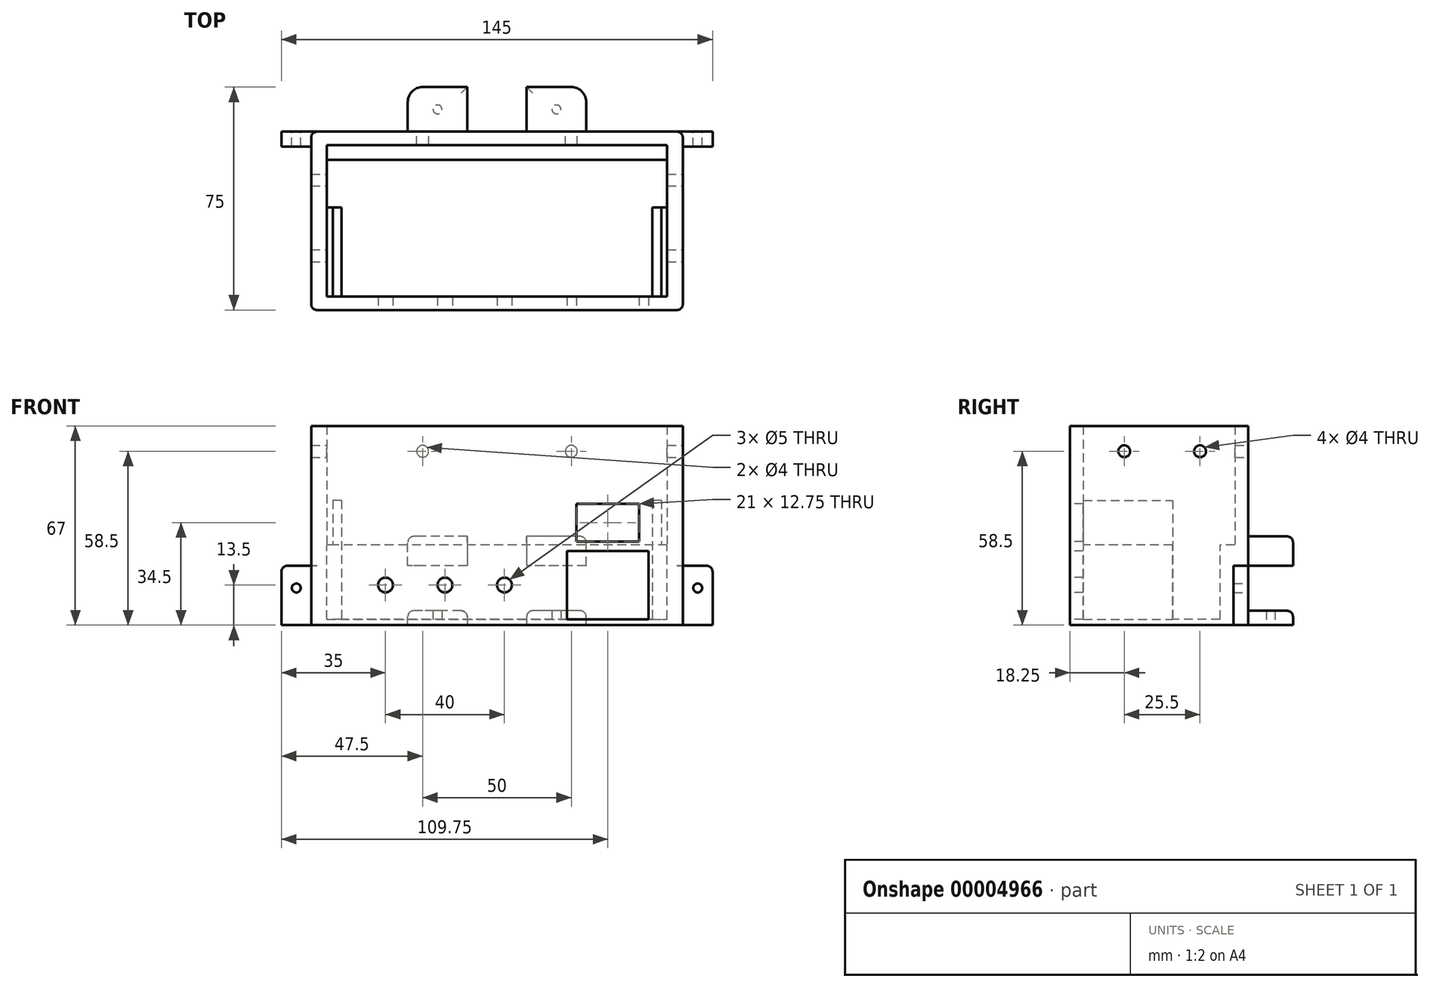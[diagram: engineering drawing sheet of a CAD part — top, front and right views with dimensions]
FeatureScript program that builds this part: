
annotation { "Feature Type Name" : "Feature", "Feature Type Description" : "" }
export const myFeature = defineFeature(function(context is Context, id is Id, definition is map)
    precondition{}
    {
        {
            var Q0;
            Q0=qCreatedBy(makeId("Top.planeOp"),FACE);
            var sketch = newSketch(context, id + "F0", { "sketchPlane" : qUnion([Q0])});
            skLineSegment(sketch, "E0.rect.bottom", {"start": v(57.25, 25.5) * mm, "end": v(-57.25, 25.5) * mm});
            skLineSegment(sketch, "E0.rect.top", {"start": v(57.25, -25.5) * mm, "end": v(-57.25, -25.5) * mm});
            skLineSegment(sketch, "E0.rect.left", {"start": v(57.25, 25.5) * mm, "end": v(57.25, -25.5) * mm});
            skLineSegment(sketch, "E0.rect.right", {"start": v(-57.25, 25.5) * mm, "end": v(-57.25, -25.5) * mm});
            skPoint(sketch, "E0.rect.middle", {"position": v(0, 0) * mm});
            skLineSegment(sketch, "E1.rect.bottom", {"start": v(62.5, 30) * mm, "end": v(-62.5, 30) * mm});
            skLineSegment(sketch, "E1.rect.top", {"start": v(62.5, -30) * mm, "end": v(-62.5, -30) * mm});
            skLineSegment(sketch, "E1.rect.left", {"start": v(62.5, 30) * mm, "end": v(62.5, -30) * mm});
            skLineSegment(sketch, "E1.rect.right", {"start": v(-62.5, 30) * mm, "end": v(-62.5, -30) * mm});
            skSolve(sketch);
        }
        {
            var Q0;
            Q0 = qSketchRegion(id + "F0", true);
            extrude(context, id + "F1", {"entities" : qUnion([Q0]), "depth" : 40 * mm});
        }
        {
            var Q0;
            Q0=makeQuery(id+"F1.opExtrude","CAP_FACE",FACE,{"disambiguationData":[OSD([sQuery(id+"F0.wireOp",EDGE,"E0.rect.bottom"),sQuery(id+"F0.wireOp",EDGE,"E0.rect.top"),sQuery(id+"F0.wireOp",EDGE,"E0.rect.left"),sQuery(id+"F0.wireOp",EDGE,"E0.rect.right"),sQuery(id+"F0.wireOp",EDGE,"E1.rect.bottom"),sQuery(id+"F0.wireOp",EDGE,"E1.rect.top"),sQuery(id+"F0.wireOp",EDGE,"E1.rect.left"),sQuery(id+"F0.wireOp",EDGE,"E1.rect.right")])],"isStart":true});
            var sketch = newSketch(context, id + "F2", { "sketchPlane" : qUnion([Q0])});
            skLineSegment(sketch, "E2", {"start": v(0, 0) * mm, "end": v(0, 25.5) * mm, "construction": true});
            skLineSegment(sketch, "E3.bottom", {"start": v(-55.25, 25.5) * mm, "end": v(-52.25, 25.5) * mm});
            skLineSegment(sketch, "E3.top", {"start": v(-55.25, -4.5) * mm, "end": v(-52.25, -4.5) * mm});
            skLineSegment(sketch, "E3.left", {"start": v(-55.25, 25.5) * mm, "end": v(-55.25, -4.5) * mm});
            skLineSegment(sketch, "E3.right", {"start": v(-52.25, 25.5) * mm, "end": v(-52.25, -4.5) * mm});
            skLineSegment(sketch, "E4.0.MirrorCS", {"start": v(52.25, 25.5) * mm, "end": v(52.25, -4.5) * mm});
            skLineSegment(sketch, "E4.1.MirrorCS", {"start": v(55.25, 25.5) * mm, "end": v(55.25, -4.5) * mm});
            skLineSegment(sketch, "E4.2.MirrorCS", {"start": v(55.25, -4.5) * mm, "end": v(52.25, -4.5) * mm});
            skLineSegment(sketch, "E4.3.MirrorCS", {"start": v(55.25, 25.5) * mm, "end": v(52.25, 25.5) * mm});
            skSolve(sketch);
        }
        {
            var Q0;
            Q0 = qSketchRegion(id + "F2", true);
            extrude(context, id + "F3", {"entities" : qUnion([Q0]), "operationType" : NewBodyOperationType.ADD, "oppositeDirection" : true, "depth" : 15 * mm});
        }
        {
            var Q0;
            Q0=makeQuery(id+"F3.boolean.opBoolean","MERGE",FACE,{"derivedFrom":[makeQuery(id+"F1.opExtrude","CAP_FACE",FACE,{"disambiguationData":[OSD([sQuery(id+"F0.wireOp",EDGE,"E0.rect.bottom"),sQuery(id+"F0.wireOp",EDGE,"E0.rect.top"),sQuery(id+"F0.wireOp",EDGE,"E0.rect.left"),sQuery(id+"F0.wireOp",EDGE,"E0.rect.right"),sQuery(id+"F0.wireOp",EDGE,"E1.rect.bottom"),sQuery(id+"F0.wireOp",EDGE,"E1.rect.top"),sQuery(id+"F0.wireOp",EDGE,"E1.rect.left"),sQuery(id+"F0.wireOp",EDGE,"E1.rect.right")])],"isStart":true}),makeQuery(id+"F3.opExtrude","CAP_FACE",FACE,{"disambiguationData":[OSD([sQuery(id+"F2.wireOp",EDGE,"E3.bottom"),sQuery(id+"F2.wireOp",EDGE,"E3.top"),sQuery(id+"F2.wireOp",EDGE,"E3.left"),sQuery(id+"F2.wireOp",EDGE,"E3.right")])],"isStart":true}),makeQuery(id+"F3.opExtrude","CAP_FACE",FACE,{"disambiguationData":[OSD([sQuery(id+"F2.wireOp",EDGE,"E4.0.MirrorCS"),sQuery(id+"F2.wireOp",EDGE,"E4.1.MirrorCS"),sQuery(id+"F2.wireOp",EDGE,"E4.2.MirrorCS"),sQuery(id+"F2.wireOp",EDGE,"E4.3.MirrorCS")])],"isStart":true})]});
            var sketch = newSketch(context, id + "F4", { "sketchPlane" : qUnion([Q0])});
            skLineSegment(sketch, "E5.0", {"start": v(62.5, 30) * mm, "end": v(-62.5, 30) * mm});
            skLineSegment(sketch, "E5.1", {"start": v(-62.5, -30) * mm, "end": v(-62.5, 30) * mm});
            skLineSegment(sketch, "E5.2", {"start": v(62.5, -30) * mm, "end": v(-62.5, -30) * mm});
            skLineSegment(sketch, "E5.3", {"start": v(62.5, -30) * mm, "end": v(62.5, 30) * mm});
            skLineSegment(sketch, "E6.0", {"start": v(52.25, 25.5) * mm, "end": v(-52.25, 25.5) * mm});
            skLineSegment(sketch, "E6.1", {"start": v(-52.25, 25.5) * mm, "end": v(-52.25, -4.5) * mm});
            skLineSegment(sketch, "E6.2", {"start": v(52.25, 25.5) * mm, "end": v(52.25, -4.5) * mm});
            skLineSegment(sketch, "E7", {"start": v(-52.25, -4.5) * mm, "end": v(-57.25, -4.5) * mm});
            skLineSegment(sketch, "E8", {"start": v(52.25, -4.5) * mm, "end": v(57.25, -4.5) * mm});
            skLineSegment(sketch, "E9", {"start": v(-57.25, -20.5) * mm, "end": v(57.25, -20.5) * mm});
            skLineSegment(sketch, "E10", {"start": v(57.25, -20.5) * mm, "end": v(57.25, -4.5) * mm});
            skLineSegment(sketch, "E11", {"start": v(-57.25, -4.5) * mm, "end": v(-57.25, -20.5) * mm});
            skSolve(sketch);
        }
        {
            var Q0;
            Q0 = qSketchRegion(id + "F4", true);
            extrude(context, id + "F5", {"entities" : qUnion([Q0]), "operationType" : NewBodyOperationType.ADD, "depth" : 25 * mm});
        }
        {
            var Q0;
            Q0=makeQuery(id+"F5.opExtrude","CAP_FACE",FACE,{"disambiguationData":[OSD([sQuery(id+"F4.wireOp",EDGE,"E5.0"),sQuery(id+"F4.wireOp",EDGE,"E5.1"),sQuery(id+"F4.wireOp",EDGE,"E5.2"),sQuery(id+"F4.wireOp",EDGE,"E5.3"),sQuery(id+"F4.wireOp",EDGE,"E6.0"),sQuery(id+"F4.wireOp",EDGE,"E6.1"),sQuery(id+"F4.wireOp",EDGE,"E6.2"),sQuery(id+"F4.wireOp",EDGE,"E6.3"),sQuery(id+"F4.wireOp",EDGE,"E7"),sQuery(id+"F4.wireOp",EDGE,"ebbf834a-ca51-483e-9cb7-4b44b67fc53c"),sQuery(id+"F4.wireOp",EDGE,"E8"),sQuery(id+"F4.wireOp",EDGE,"05d7400e-08cb-4981-ba75-3c27e8bfba8a")])],"isStart":false});
            var sketch = newSketch(context, id + "F6", { "sketchPlane" : qUnion([Q0])});
            skLineSegment(sketch, "E12.0", {"start": v(62.5, 30) * mm, "end": v(-62.5, 30) * mm});
            skLineSegment(sketch, "E12.1", {"start": v(-62.5, -30) * mm, "end": v(-62.5, 30) * mm});
            skLineSegment(sketch, "E12.2", {"start": v(62.5, -30) * mm, "end": v(-62.5, -30) * mm});
            skLineSegment(sketch, "E12.3", {"start": v(62.5, -30) * mm, "end": v(62.5, 30) * mm});
            skSolve(sketch);
        }
        {
            var Q0;
            Q0 = qSketchRegion(id + "F6", true);
            extrude(context, id + "F7", {"entities" : qUnion([Q0]), "operationType" : NewBodyOperationType.ADD, "depth" : 2 * mm});
        }
        {
            var Q0;
            Q0=makeQuery(id+"F7.boolean.opBoolean","MERGE",FACE,{"derivedFrom":[makeQuery(id+"F5.boolean.opBoolean","MERGE",FACE,{"derivedFrom":[makeQuery(id+"F1.opExtrude","SWEPT_FACE",FACE,{"disambiguationData":[OSD([sQuery(id+"F0.wireOp",EDGE,"E1.rect.top")])]}),makeQuery(id+"F5.opExtrude","SWEPT_FACE",FACE,{"disambiguationData":[OSD([sQuery(id+"F4.wireOp",EDGE,"E5.0")])]})]}),makeQuery(id+"F7.opExtrude","SWEPT_FACE",FACE,{"disambiguationData":[OSD([sQuery(id+"F6.wireOp",EDGE,"E12.0")])]})]});
            var sketch = newSketch(context, id + "F8", { "sketchPlane" : qUnion([Q0])});
            skLineSegment(sketch, "E13.0", {"start": v(55.25, 15) * mm, "end": v(52.25, 15) * mm, "construction": true});
            skLineSegment(sketch, "E14.0", {"start": v(-57.25, -25) * mm, "end": v(57.25, -25) * mm, "construction": true});
            skLineSegment(sketch, "E15.bottom", {"start": v(52.25, -25) * mm, "end": v(22.25, -25) * mm, "construction": true});
            skLineSegment(sketch, "E15.top", {"start": v(52.25, -2) * mm, "end": v(22.25, -2) * mm, "construction": true});
            skLineSegment(sketch, "E15.left", {"start": v(52.25, -25) * mm, "end": v(52.25, -2) * mm, "construction": true});
            skLineSegment(sketch, "E15.right", {"start": v(22.25, -25) * mm, "end": v(22.25, -2) * mm, "construction": true});
            skLineSegment(sketch, "E16.bottom", {"start": v(47.75, 0) * mm, "end": v(26.75, 0) * mm, "construction": true});
            skLineSegment(sketch, "E16.top", {"start": v(47.75, 15) * mm, "end": v(26.75, 15) * mm, "construction": true});
            skLineSegment(sketch, "E16.left", {"start": v(47.75, 0) * mm, "end": v(47.75, 15) * mm, "construction": true});
            skLineSegment(sketch, "E16.right", {"start": v(26.75, 0) * mm, "end": v(26.75, 15) * mm, "construction": true});
            skLineSegment(sketch, "E17", {"start": v(37.25, 0) * mm, "end": v(37.25, -2) * mm, "construction": true});
            skLineSegment(sketch, "E18.bottom", {"start": v(23.5, -2) * mm, "end": v(51, -2) * mm});
            skLineSegment(sketch, "E18.top", {"start": v(23.5, -25) * mm, "end": v(51, -25) * mm});
            skLineSegment(sketch, "E18.left", {"start": v(23.5, -2) * mm, "end": v(23.5, -25) * mm});
            skLineSegment(sketch, "E18.right", {"start": v(51, -2) * mm, "end": v(51, -25) * mm});
            skPoint(sketch, "E19", {"position": v(26.75, 7.5) * mm});
            skLineSegment(sketch, "E20.bottom", {"start": v(26.75, 13.88) * mm, "end": v(47.75, 13.88) * mm});
            skLineSegment(sketch, "E20.top", {"start": v(26.75, 1.13) * mm, "end": v(47.75, 1.13) * mm});
            skLineSegment(sketch, "E20.left", {"start": v(26.75, 13.88) * mm, "end": v(26.75, 1.13) * mm});
            skLineSegment(sketch, "E20.right", {"start": v(47.75, 13.88) * mm, "end": v(47.75, 1.13) * mm});
            skLineSegment(sketch, "E21", {"start": v(22.25, -13.5) * mm, "end": v(-57.25, -13.5) * mm, "construction": true});
            skCircle(sketch, "E22", {"center": v(-17.5, -13.5) * mm, "radius": 2.5 * mm});
            skCircle(sketch, "E23", {"center": v(-37.5, -13.5) * mm, "radius": 2.5 * mm});
            skLineSegment(sketch, "E24", {"start": v(-17.5, -13.5) * mm, "end": v(-17.5, 13.54) * mm, "construction": true});
            skCircle(sketch, "E25.0.MirrorC", {"center": v(2.5, -13.5) * mm, "radius": 2.5 * mm});
            skSolve(sketch);
        }
        {
            var Q0;
            Q0 = qSketchRegion(id + "F8", true);
            var Q1;
            Q1=makeQuery(id+"F5.boolean.opBoolean","MERGE",FACE,{"derivedFrom":[makeQuery(id+"F1.opExtrude","SWEPT_FACE",FACE,{"disambiguationData":[OSD([sQuery(id+"F0.wireOp",EDGE,"E0.rect.top")])]}),makeQuery(id+"F5.opExtrude","SWEPT_FACE",FACE,{"disambiguationData":[OSD([sQuery(id+"F4.wireOp",EDGE,"E6.0")])]})]});
            extrude(context, id + "F9", {"entities" : qUnion([Q0]), "operationType" : NewBodyOperationType.REMOVE, "endBound" : BoundingType.UP_TO_SURFACE, "oppositeDirection" : true, "endBoundEntityFace" : qUnion([Q1]), "depth" : 25 * mm});
        }
        {
            var Q0;
            Q0=makeQuery(id+"F7.boolean.opBoolean","MERGE",FACE,{"derivedFrom":[makeQuery(id+"F5.boolean.opBoolean","MERGE",FACE,{"derivedFrom":[makeQuery(id+"F1.opExtrude","SWEPT_FACE",FACE,{"disambiguationData":[OSD([sQuery(id+"F0.wireOp",EDGE,"E1.rect.left")])]}),makeQuery(id+"F5.opExtrude","SWEPT_FACE",FACE,{"disambiguationData":[OSD([sQuery(id+"F4.wireOp",EDGE,"E5.3")])]})]}),makeQuery(id+"F7.opExtrude","SWEPT_FACE",FACE,{"disambiguationData":[OSD([sQuery(id+"F6.wireOp",EDGE,"E12.3")])]})]});
            var sketch = newSketch(context, id + "F10", { "sketchPlane" : qUnion([Q0])});
            skLineSegment(sketch, "E26.0", {"start": v(4.5, 0) * mm, "end": v(-25.5, 0) * mm, "construction": true});
            skLineSegment(sketch, "E27", {"start": v(-25.5, 31.5) * mm, "end": v(25.5, 31.5) * mm, "construction": true});
            skLineSegment(sketch, "E28.0", {"start": v(25.5, 40) * mm, "end": v(25.5, 0) * mm, "construction": true});
            skLineSegment(sketch, "E29.0", {"start": v(-25.5, 40) * mm, "end": v(-25.5, 0) * mm, "construction": true});
            skCircle(sketch, "E30", {"center": v(-11.75, 31.5) * mm, "radius": 2 * mm});
            skCircle(sketch, "E31", {"center": v(13.75, 31.5) * mm, "radius": 2 * mm});
            skSolve(sketch);
        }
        {
            var Q0;
            Q0 = qSketchRegion(id + "F10", true);
            extrude(context, id + "F11", {"entities" : qUnion([Q0]), "operationType" : NewBodyOperationType.REMOVE, "endBound" : BoundingType.THROUGH_ALL, "oppositeDirection" : true, "depth" : 25 * mm});
        }
        {
            var Q0;
            Q0=makeQuery(id+"F7.boolean.opBoolean","MERGE",FACE,{"derivedFrom":[makeQuery(id+"F5.boolean.opBoolean","MERGE",FACE,{"derivedFrom":[makeQuery(id+"F1.opExtrude","SWEPT_FACE",FACE,{"disambiguationData":[OSD([sQuery(id+"F0.wireOp",EDGE,"E1.rect.bottom")])]}),makeQuery(id+"F5.opExtrude","SWEPT_FACE",FACE,{"disambiguationData":[OSD([sQuery(id+"F4.wireOp",EDGE,"E5.2")])]})]}),makeQuery(id+"F7.opExtrude","SWEPT_FACE",FACE,{"disambiguationData":[OSD([sQuery(id+"F6.wireOp",EDGE,"E12.2")])]})]});
            var sketch = newSketch(context, id + "F12", { "sketchPlane" : qUnion([Q0])});
            skLineSegment(sketch, "E32.0", {"start": v(-62.5, 29.5) * mm, "end": v(-62.5, 33.5) * mm, "construction": true});
            skLineSegment(sketch, "E33", {"start": v(-62.5, 31.5) * mm, "end": v(62.5, 31.5) * mm, "construction": true});
            skLineSegment(sketch, "E34", {"start": v(0, 31.5) * mm, "end": v(0, -3.55) * mm, "construction": true});
            skCircle(sketch, "E35", {"center": v(-25, 31.5) * mm, "radius": 2 * mm});
            skCircle(sketch, "E36.0.MirrorC", {"center": v(25, 31.5) * mm, "radius": 2 * mm});
            skSolve(sketch);
        }
        {
            var Q0;
            Q0 = qSketchRegion(id + "F12", true);
            var Q1;
            Q1=makeQuery(id+"F1.opExtrude","SWEPT_FACE",FACE,{"disambiguationData":[OSD([sQuery(id+"F0.wireOp",EDGE,"E0.rect.bottom")])]});
            extrude(context, id + "F13", {"entities" : qUnion([Q0]), "operationType" : NewBodyOperationType.REMOVE, "endBound" : BoundingType.UP_TO_SURFACE, "oppositeDirection" : true, "endBoundEntityFace" : qUnion([Q1]), "depth" : 25 * mm});
        }
        {
            var Q0;
            Q0=makeQuery(id+"F7.boolean.opBoolean","MERGE",FACE,{"derivedFrom":[makeQuery(id+"F5.boolean.opBoolean","MERGE",FACE,{"derivedFrom":[makeQuery(id+"F1.opExtrude","SWEPT_FACE",FACE,{"disambiguationData":[OSD([sQuery(id+"F0.wireOp",EDGE,"E1.rect.bottom")])]}),makeQuery(id+"F5.opExtrude","SWEPT_FACE",FACE,{"disambiguationData":[OSD([sQuery(id+"F4.wireOp",EDGE,"E5.2")])]})]}),makeQuery(id+"F7.opExtrude","SWEPT_FACE",FACE,{"disambiguationData":[OSD([sQuery(id+"F6.wireOp",EDGE,"E12.2")])]})]});
            var sketch = newSketch(context, id + "F14", { "sketchPlane" : qUnion([Q0])});
            skLineSegment(sketch, "E37", {"start": v(0, 40) * mm, "end": v(0, -27) * mm, "construction": true});
            skLineSegment(sketch, "E38.bottom", {"start": v(-30, -27) * mm, "end": v(30, -27) * mm});
            skLineSegment(sketch, "E38.top", {"start": v(-30, -22.15) * mm, "end": v(30, -22.15) * mm});
            skLineSegment(sketch, "E38.left", {"start": v(-30, -27) * mm, "end": v(-30, -22.15) * mm});
            skLineSegment(sketch, "E38.right", {"start": v(30, -27) * mm, "end": v(30, -22.15) * mm});
            skLineSegment(sketch, "E39.bottom", {"start": v(-30, -7) * mm, "end": v(30, -7) * mm});
            skLineSegment(sketch, "E39.top", {"start": v(-30, 2.85) * mm, "end": v(30, 2.85) * mm});
            skLineSegment(sketch, "E39.left", {"start": v(-30, -7) * mm, "end": v(-30, 2.85) * mm});
            skLineSegment(sketch, "E39.right", {"start": v(30, -7) * mm, "end": v(30, 2.85) * mm});
            skSolve(sketch);
        }
        {
            var Q0;
            Q0 = qSketchRegion(id + "F14", true);
            extrude(context, id + "F15", {"entities" : qUnion([Q0]), "operationType" : NewBodyOperationType.ADD, "depth" : 15 * mm});
        }
        {
            var Q0;
            Q0=makeQuery(id+"F15.boolean.opBoolean","MERGE",FACE,{"derivedFrom":[makeQuery(id+"F7.opExtrude","CAP_FACE",FACE,{"disambiguationData":[OSD([sQuery(id+"F6.wireOp",EDGE,"E12.0"),sQuery(id+"F6.wireOp",EDGE,"E12.1"),sQuery(id+"F6.wireOp",EDGE,"E12.2"),sQuery(id+"F6.wireOp",EDGE,"E12.3")])],"isStart":false}),makeQuery(id+"F15.opExtrude","SWEPT_FACE",FACE,{"disambiguationData":[OSD([sQuery(id+"F14.wireOp",EDGE,"E38.bottom")])]})]});
            var sketch = newSketch(context, id + "F16", { "sketchPlane" : qUnion([Q0])});
            skLineSegment(sketch, "E40", {"start": v(30, -37.5) * mm, "end": v(-30, -37.5) * mm, "construction": true});
            skCircle(sketch, "E41", {"center": v(20, -37.5) * mm, "radius": 1.5 * mm});
            skLineSegment(sketch, "E42", {"start": v(0, -37.5) * mm, "end": v(0, -45) * mm, "construction": true});
            skCircle(sketch, "E43.0.MirrorC", {"center": v(-20, -37.5) * mm, "radius": 1.5 * mm});
            skSolve(sketch);
        }
        {
            var Q0;
            Q0 = qSketchRegion(id + "F16", true);
            var Q1;
            Q1=makeQuery(id+"F15.opExtrude","SWEPT_FACE",FACE,{"disambiguationData":[OSD([sQuery(id+"F14.wireOp",EDGE,"E38.top")])]});
            extrude(context, id + "F17", {"entities" : qUnion([Q0]), "operationType" : NewBodyOperationType.REMOVE, "endBound" : BoundingType.UP_TO_SURFACE, "oppositeDirection" : true, "endBoundEntityFace" : qUnion([Q1]), "depth" : 25 * mm});
        }
        {
            var Q0;
            Q0=makeQuery(id+"F15.opExtrude","CAP_EDGE",EDGE,{"disambiguationData":[OSD([sQuery(id+"F14.wireOp",EDGE,"E39.left")])],"isStart":false});
            var Q1;
            Q1=makeQuery(id+"F15.opExtrude","CAP_EDGE",EDGE,{"disambiguationData":[OSD([sQuery(id+"F14.wireOp",EDGE,"E39.right")])],"isStart":false});
            var Q2;
            Q2=makeQuery(id+"F15.opExtrude","CAP_EDGE",EDGE,{"disambiguationData":[OSD([sQuery(id+"F14.wireOp",EDGE,"E38.right")])],"isStart":false});
            var Q3;
            Q3=makeQuery(id+"F15.opExtrude","CAP_EDGE",EDGE,{"disambiguationData":[OSD([sQuery(id+"F14.wireOp",EDGE,"E38.left")])],"isStart":false});
            fillet(context, id + "F18", {"entities" : qUnion([Q0, Q1, Q2, Q3]), "radius" : 5 * mm, "tangentPropagation" : true, "allowEdgeOverflow" : false});
        }
        {
            var Q0;
            Q0=makeQuery(id+"F15.boolean.opBoolean","MERGE",FACE,{"derivedFrom":[makeQuery(id+"F7.opExtrude","CAP_FACE",FACE,{"disambiguationData":[OSD([sQuery(id+"F6.wireOp",EDGE,"E12.0"),sQuery(id+"F6.wireOp",EDGE,"E12.1"),sQuery(id+"F6.wireOp",EDGE,"E12.2"),sQuery(id+"F6.wireOp",EDGE,"E12.3")])],"isStart":false}),makeQuery(id+"F15.opExtrude","SWEPT_FACE",FACE,{"disambiguationData":[OSD([sQuery(id+"F14.wireOp",EDGE,"E38.bottom")])]})]});
            var sketch = newSketch(context, id + "F19", { "sketchPlane" : qUnion([Q0])});
            skLineSegment(sketch, "E44", {"start": v(0, -45) * mm, "end": v(0, -7.23) * mm, "construction": true});
            skLineSegment(sketch, "E45.bottom", {"start": v(10, -45) * mm, "end": v(-10, -45) * mm});
            skLineSegment(sketch, "E45.top", {"start": v(10, -30) * mm, "end": v(-10, -30) * mm});
            skLineSegment(sketch, "E45.left", {"start": v(10, -45) * mm, "end": v(10, -30) * mm});
            skLineSegment(sketch, "E45.right", {"start": v(-10, -45) * mm, "end": v(-10, -30) * mm});
            skSolve(sketch);
        }
        {
            var Q0;
            Q0 = qSketchRegion(id + "F19", true);
            var Q1;
            Q1=makeQuery(id+"F15.opExtrude","SWEPT_FACE",FACE,{"disambiguationData":[OSD([sQuery(id+"F14.wireOp",EDGE,"E39.top")])]});
            extrude(context, id + "F20", {"entities" : qUnion([Q0]), "operationType" : NewBodyOperationType.REMOVE, "endBound" : BoundingType.UP_TO_SURFACE, "oppositeDirection" : true, "endBoundEntityFace" : qUnion([Q1]), "depth" : 25 * mm});
        }
        {
            var Q0;
            Q0=makeQuery(id+"F20.boolean.opBoolean","MERGE",FACE,{"derivedFrom":[makeQuery(id+"F7.boolean.opBoolean","MERGE",FACE,{"derivedFrom":[makeQuery(id+"F5.boolean.opBoolean","MERGE",FACE,{"derivedFrom":[makeQuery(id+"F1.opExtrude","SWEPT_FACE",FACE,{"disambiguationData":[OSD([sQuery(id+"F0.wireOp",EDGE,"E1.rect.bottom")])]}),makeQuery(id+"F5.opExtrude","SWEPT_FACE",FACE,{"disambiguationData":[OSD([sQuery(id+"F4.wireOp",EDGE,"E5.2")])]})]}),makeQuery(id+"F7.opExtrude","SWEPT_FACE",FACE,{"disambiguationData":[OSD([sQuery(id+"F6.wireOp",EDGE,"E12.2")])]})]}),makeQuery(id+"F20.opExtrude","SWEPT_FACE",FACE,{"disambiguationData":[OSD([sQuery(id+"F19.wireOp",EDGE,"E45.top")])]})]});
            var sketch = newSketch(context, id + "F21", { "sketchPlane" : qUnion([Q0])});
            skLineSegment(sketch, "E46", {"start": v(0, 40) * mm, "end": v(0, 5.46) * mm, "construction": true});
            skLineSegment(sketch, "E47.bottom", {"start": v(62.5, -27) * mm, "end": v(72.5, -27) * mm});
            skLineSegment(sketch, "E47.top", {"start": v(62.5, -7) * mm, "end": v(72.5, -7) * mm});
            skLineSegment(sketch, "E47.left", {"start": v(62.5, -27) * mm, "end": v(62.5, -7) * mm});
            skLineSegment(sketch, "E47.right", {"start": v(72.5, -27) * mm, "end": v(72.5, -7) * mm});
            skLineSegment(sketch, "E48", {"start": v(67.5, -7) * mm, "end": v(67.5, -27) * mm, "construction": true});
            skCircle(sketch, "E49", {"center": v(67.5, -14.5) * mm, "radius": 1.5 * mm});
            skCircle(sketch, "E50.0.MirrorC", {"center": v(-67.5, -14.5) * mm, "radius": 1.5 * mm});
            skLineSegment(sketch, "E50.1.MirrorCS", {"start": v(-72.5, -27) * mm, "end": v(-72.5, -7) * mm});
            skLineSegment(sketch, "E50.2.MirrorCS", {"start": v(-62.5, -27) * mm, "end": v(-72.5, -27) * mm});
            skLineSegment(sketch, "E50.3.MirrorCS", {"start": v(-62.5, -27) * mm, "end": v(-62.5, -7) * mm});
            skLineSegment(sketch, "E50.4.MirrorCS", {"start": v(-62.5, -7) * mm, "end": v(-72.5, -7) * mm});
            skSolve(sketch);
        }
        {
            var Q0;
            Q0 = qSketchRegion(id + "F21", true);
            extrude(context, id + "F22", {"entities" : qUnion([Q0]), "operationType" : NewBodyOperationType.ADD, "oppositeDirection" : true, "depth" : 5 * mm});
        }
        {
            var Q0;
            Q0=makeQuery(id+"F15.opExtrude","SWEPT_EDGE",EDGE,{"disambiguationData":[OSD([sQuery(id+"F14.wireOp",EDGE,"E39.top"),sQuery(id+"F14.wireOp",EDGE,"E39.left")])]});
            var Q1;
            Q1=makeQuery(id+"F15.opExtrude","SWEPT_EDGE",EDGE,{"disambiguationData":[OSD([sQuery(id+"F14.wireOp",EDGE,"E38.top"),sQuery(id+"F14.wireOp",EDGE,"E38.left")])]});
            var Q2;
            Q2=makeQuery(id+"F7.boolean.opBoolean","MERGE",EDGE,{"derivedFrom":[makeQuery(id+"F5.boolean.opBoolean","MERGE",EDGE,{"derivedFrom":[makeQuery(id+"F1.opExtrude","SWEPT_EDGE",EDGE,{"disambiguationData":[OSD([sQuery(id+"F0.wireOp",EDGE,"E1.rect.top"),sQuery(id+"F0.wireOp",EDGE,"E1.rect.left")])]}),makeQuery(id+"F5.opExtrude","SWEPT_EDGE",EDGE,{"disambiguationData":[OSD([sQuery(id+"F4.wireOp",EDGE,"E5.0"),sQuery(id+"F4.wireOp",EDGE,"E5.3")])]})]}),makeQuery(id+"F7.opExtrude","SWEPT_EDGE",EDGE,{"disambiguationData":[OSD([sQuery(id+"F6.wireOp",EDGE,"E12.0"),sQuery(id+"F6.wireOp",EDGE,"E12.3")])]})]});
            var Q3;
            Q3=makeQuery(id+"F7.boolean.opBoolean","MERGE",EDGE,{"derivedFrom":[makeQuery(id+"F5.boolean.opBoolean","MERGE",EDGE,{"derivedFrom":[makeQuery(id+"F1.opExtrude","SWEPT_EDGE",EDGE,{"disambiguationData":[OSD([sQuery(id+"F0.wireOp",EDGE,"E1.rect.bottom"),sQuery(id+"F0.wireOp",EDGE,"E1.rect.left")])]}),makeQuery(id+"F5.opExtrude","SWEPT_EDGE",EDGE,{"disambiguationData":[OSD([sQuery(id+"F4.wireOp",EDGE,"E5.2"),sQuery(id+"F4.wireOp",EDGE,"E5.3")])]})]}),makeQuery(id+"F7.opExtrude","SWEPT_EDGE",EDGE,{"disambiguationData":[OSD([sQuery(id+"F6.wireOp",EDGE,"E12.2"),sQuery(id+"F6.wireOp",EDGE,"E12.3")])]})]});
            var Q4;
            Q4=makeQuery(id+"F7.boolean.opBoolean","MERGE",EDGE,{"derivedFrom":[makeQuery(id+"F5.boolean.opBoolean","MERGE",EDGE,{"derivedFrom":[makeQuery(id+"F1.opExtrude","SWEPT_EDGE",EDGE,{"disambiguationData":[OSD([sQuery(id+"F0.wireOp",EDGE,"E1.rect.bottom"),sQuery(id+"F0.wireOp",EDGE,"E1.rect.right")])]}),makeQuery(id+"F5.opExtrude","SWEPT_EDGE",EDGE,{"disambiguationData":[OSD([sQuery(id+"F4.wireOp",EDGE,"E5.1"),sQuery(id+"F4.wireOp",EDGE,"E5.2")])]})]}),makeQuery(id+"F7.opExtrude","SWEPT_EDGE",EDGE,{"disambiguationData":[OSD([sQuery(id+"F6.wireOp",EDGE,"E12.1"),sQuery(id+"F6.wireOp",EDGE,"E12.2")])]})]});
            var Q5;
            Q5=makeQuery(id+"F7.boolean.opBoolean","MERGE",EDGE,{"derivedFrom":[makeQuery(id+"F5.boolean.opBoolean","MERGE",EDGE,{"derivedFrom":[makeQuery(id+"F1.opExtrude","SWEPT_EDGE",EDGE,{"disambiguationData":[OSD([sQuery(id+"F0.wireOp",EDGE,"E1.rect.top"),sQuery(id+"F0.wireOp",EDGE,"E1.rect.right")])]}),makeQuery(id+"F5.opExtrude","SWEPT_EDGE",EDGE,{"disambiguationData":[OSD([sQuery(id+"F4.wireOp",EDGE,"E5.0"),sQuery(id+"F4.wireOp",EDGE,"E5.1")])]})]}),makeQuery(id+"F7.opExtrude","SWEPT_EDGE",EDGE,{"disambiguationData":[OSD([sQuery(id+"F6.wireOp",EDGE,"E12.0"),sQuery(id+"F6.wireOp",EDGE,"E12.1")])]})]});
            var Q6;
            Q6=makeQuery(id+"F20.boolean.opBoolean","COPY",EDGE,{"derivedFrom":makeQuery(id+"F20.opExtrude","CAP_EDGE",EDGE,{"disambiguationData":[OSD([sQuery(id+"F19.wireOp",EDGE,"E45.left")])],"isStart":false})});
            var Q7;
            Q7=makeQuery(id+"F20.boolean.opBoolean","COPY",EDGE,{"derivedFrom":makeQuery(id+"F20.opExtrude","CAP_EDGE",EDGE,{"disambiguationData":[OSD([sQuery(id+"F19.wireOp",EDGE,"E45.right")])],"isStart":false})});
            var Q8;
            Q8=makeQuery(id+"F15.opExtrude","SWEPT_EDGE",EDGE,{"disambiguationData":[OSD([sQuery(id+"F14.wireOp",EDGE,"E39.top"),sQuery(id+"F14.wireOp",EDGE,"E39.right")])]});
            var Q9;
            Q9=makeQuery(id+"F15.opExtrude","SWEPT_EDGE",EDGE,{"disambiguationData":[OSD([sQuery(id+"F14.wireOp",EDGE,"E38.top"),sQuery(id+"F14.wireOp",EDGE,"E38.right")])]});
            var Q10;
            Q10=makeQuery(id+"F20.boolean.opBoolean","INTERSECT",EDGE,{"derivedFrom":[makeQuery(id+"F15.opExtrude","SWEPT_FACE",FACE,{"disambiguationData":[OSD([sQuery(id+"F14.wireOp",EDGE,"E38.top")])]}),makeQuery(id+"F20.opExtrude","SWEPT_FACE",FACE,{"disambiguationData":[OSD([sQuery(id+"F19.wireOp",EDGE,"E45.left")])]})]});
            var Q11;
            Q11=makeQuery(id+"F20.boolean.opBoolean","INTERSECT",EDGE,{"derivedFrom":[makeQuery(id+"F15.opExtrude","SWEPT_FACE",FACE,{"disambiguationData":[OSD([sQuery(id+"F14.wireOp",EDGE,"E38.top")])]}),makeQuery(id+"F20.opExtrude","SWEPT_FACE",FACE,{"disambiguationData":[OSD([sQuery(id+"F19.wireOp",EDGE,"E45.right")])]})]});
            var Q12;
            Q12=makeQuery(id+"F22.opExtrude","SWEPT_EDGE",EDGE,{"disambiguationData":[OSD([sQuery(id+"F21.wireOp",EDGE,"E47.top"),sQuery(id+"F21.wireOp",EDGE,"E47.right")])]});
            var Q13;
            Q13=makeQuery(id+"F22.opExtrude","SWEPT_EDGE",EDGE,{"disambiguationData":[OSD([sQuery(id+"F21.wireOp",EDGE,"E50.1.MirrorCS"),sQuery(id+"F21.wireOp",EDGE,"E50.4.MirrorCS")])]});
            var Q14;
            Q14=makeQuery(id+"F22.opExtrude","CAP_EDGE",EDGE,{"disambiguationData":[OSD([sQuery(id+"F21.wireOp",EDGE,"E47.left")])],"isStart":false});
            var Q15;
            Q15=makeQuery(id+"F22.opExtrude","CAP_EDGE",EDGE,{"disambiguationData":[OSD([sQuery(id+"F21.wireOp",EDGE,"E50.3.MirrorCS")])],"isStart":false});
            fillet(context, id + "F23", {"entities" : qUnion([Q0, Q1, Q2, Q3, Q4, Q5, Q6, Q7, Q8, Q9, Q10, Q11, Q12, Q13, Q14, Q15]), "radius" : 2 * mm, "tangentPropagation" : true, "allowEdgeOverflow" : false});
        }
    });
